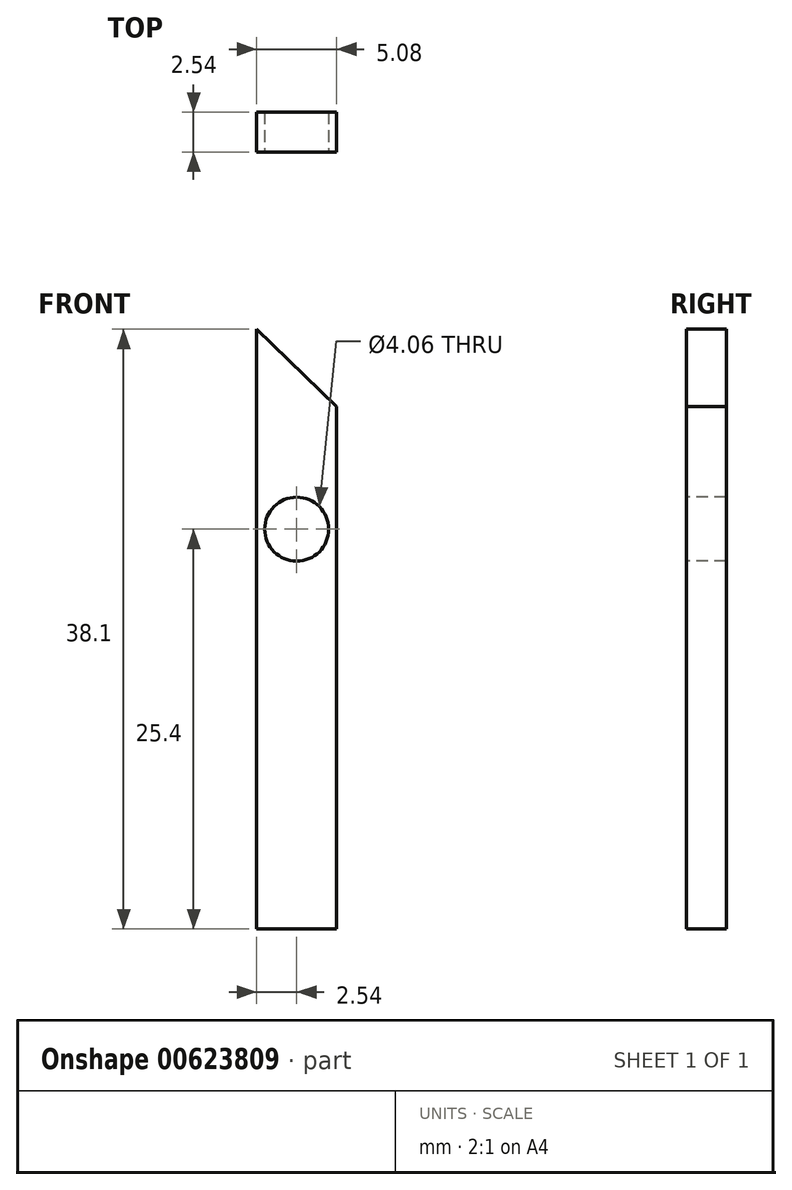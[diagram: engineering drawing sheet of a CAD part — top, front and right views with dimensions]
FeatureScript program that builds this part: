
annotation { "Feature Type Name" : "Feature", "Feature Type Description" : "" }
export const myFeature = defineFeature(function(context is Context, id is Id, definition is map)
    precondition{}
    {
        {
            var Q0;
            Q0=qCreatedBy(makeId("Front.planeOp"),FACE);
            var sketch = newSketch(context, id + "F0", { "sketchPlane" : qUnion([Q0])});
            skLineSegment(sketch, "E0.bottom", {"start": v(2.54, -19.05) * mm, "end": v(-2.54, -19.05) * mm});
            skLineSegment(sketch, "E0.top", {"start": v(2.54, 19.05) * mm, "end": v(-2.54, 19.05) * mm});
            skLineSegment(sketch, "E0.left", {"start": v(2.54, -19.05) * mm, "end": v(2.54, 19.05) * mm});
            skLineSegment(sketch, "E0.right", {"start": v(-2.54, -19.05) * mm, "end": v(-2.54, 19.05) * mm});
            skPoint(sketch, "E0.middle", {"position": v(0, 0) * mm});
            skSolve(sketch);
        }
        {
            var Q0;
            Q0 = qSketchRegion(id + "F0", true);
            extrude(context, id + "F1", {"entities" : qUnion([Q0]), "depth" : 2.54 * mm, "offsetDistance" : 25.4 * mm});
        }
        {
            var Q0;
            Q0=makeQuery(id+"F1.opExtrude","SWEPT_EDGE",EDGE,{"disambiguationData":[OSD([sQuery(id+"F0.wireOp",EDGE,"E0.top"),sQuery(id+"F0.wireOp",EDGE,"E0.left")])]});
            chamfer(context, id + "F2", {"entities" : qUnion([Q0]), "chamferType" : ChamferType.OFFSET_ANGLE, "width" : 5.08 * mm, "oppositeDirection" : false, "angle" : 44 * degree, "tangentPropagation" : true});
        }
        {
            var Q0;
            Q0=makeQuery(id+"F1.opExtrude","CAP_FACE",FACE,{"disambiguationData":[OSD([sQuery(id+"F0.wireOp",EDGE,"E0.bottom"),sQuery(id+"F0.wireOp",EDGE,"E0.top"),sQuery(id+"F0.wireOp",EDGE,"E0.left"),sQuery(id+"F0.wireOp",EDGE,"E0.right")])],"isStart":false});
            var sketch = newSketch(context, id + "F3", { "sketchPlane" : qUnion([Q0])});
            skPoint(sketch, "E1", {"position": v(0, 0) * mm});
            skLineSegment(sketch, "E2", {"start": v(0, 0) * mm, "end": v(0, 6.35) * mm});
            skCircle(sketch, "E3", {"center": v(0, 6.35) * mm, "radius": 2.03 * mm});
            skSolve(sketch);
        }
        {
            var Q0;
            Q0 = qSketchRegion(id + "F3", true);
            extrude(context, id + "F4", {"entities" : qUnion([Q0]), "operationType" : NewBodyOperationType.REMOVE, "oppositeDirection" : true, "depth" : 25.4 * mm, "offsetDistance" : 25.4 * mm});
        }
    });
